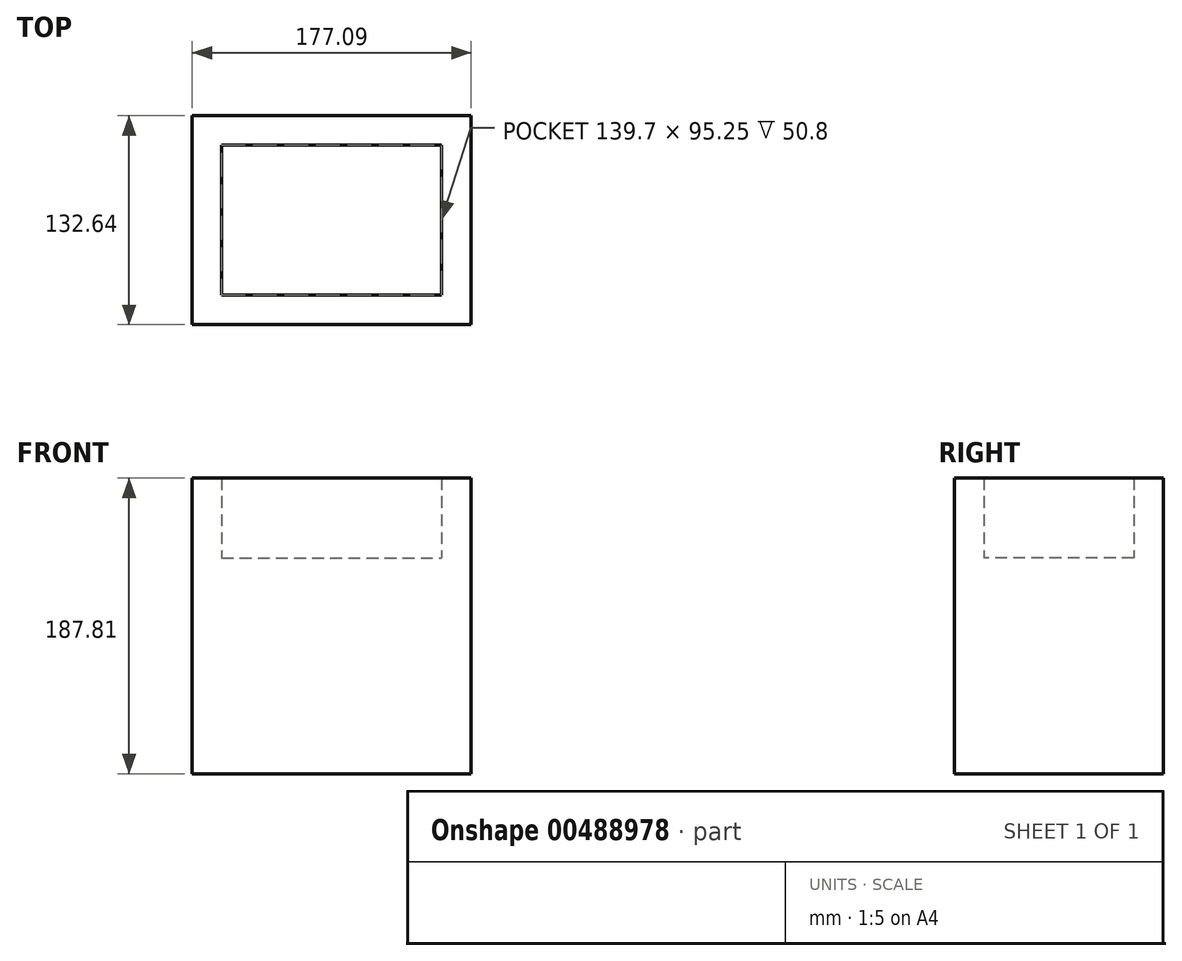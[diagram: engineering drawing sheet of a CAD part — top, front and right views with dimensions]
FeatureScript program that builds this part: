
annotation { "Feature Type Name" : "Feature", "Feature Type Description" : "" }
export const myFeature = defineFeature(function(context is Context, id is Id, definition is map)
    precondition{}
    {
        {
            var Q0;
            Q0=qCreatedBy(makeId("Top.planeOp"),FACE);
            var sketch = newSketch(context, id + "F0", { "sketchPlane" : qUnion([Q0])});
            skLineSegment(sketch, "E0", {"start": v(0, 0) * mm, "end": v(177.09, 0) * mm});
            skLineSegment(sketch, "E1", {"start": v(177.09, 0) * mm, "end": v(177.09, -132.64) * mm});
            skLineSegment(sketch, "E2", {"start": v(177.09, -132.64) * mm, "end": v(0, -132.64) * mm});
            skLineSegment(sketch, "E3", {"start": v(0, 0) * mm, "end": v(0, -132.64) * mm});
            skLineSegment(sketch, "E4", {"start": v(0, -113.94) * mm, "end": v(177.09, -113.94) * mm});
            skLineSegment(sketch, "E5", {"start": v(0, -18.7) * mm, "end": v(177.09, -18.7) * mm});
            skLineSegment(sketch, "E6", {"start": v(18.7, -18.7) * mm, "end": v(18.7, -113.94) * mm});
            skLineSegment(sketch, "E7", {"start": v(158.4, -18.7) * mm, "end": v(158.4, -113.94) * mm});
            skSolve(sketch);
        }
        {
            var Q0;
            {var subQ0=sQuery(id+"F0.wireOp",EDGE,"E6");Q0=makeQuery(id+"F0.imprint","IMPRINT",FACE,{"disambiguationData":[TD([[makeQuery(id+"F0.imprint","IMPRINT",EDGE,{"derivedFrom":subQ0}),1.0]])]});}
            extrude(context, id + "F1", {"entities" : qUnion([Q0]), "depth" : 137 * mm, "offsetDistance" : 25.4 * mm});
        }
        {
            var Q0;
            {var subQ4=sQuery(id+"F0.wireOp",EDGE,"E0");Q0=makeQuery(id+"F0.imprint","IMPRINT",FACE,{"disambiguationData":[TD([[makeQuery(id+"F0.imprint","IMPRINT",EDGE,{"derivedFrom":subQ4}),-1.0]])]});}
            var Q1;
            {var subQ5=sQuery(id+"F0.wireOp",EDGE,"E7");Q1=makeQuery(id+"F0.imprint","IMPRINT",FACE,{"disambiguationData":[TD([[makeQuery(id+"F0.imprint","IMPRINT",EDGE,{"derivedFrom":subQ5}),1.0]])]});}
            var Q2;
            {var subQ1=sQuery(id+"F0.wireOp",EDGE,"E2");Q2=makeQuery(id+"F0.imprint","IMPRINT",FACE,{"disambiguationData":[TD([[makeQuery(id+"F0.imprint","IMPRINT",EDGE,{"derivedFrom":subQ1}),-1.0]])]});}
            var Q3;
            {var subQ5=sQuery(id+"F0.wireOp",EDGE,"E6");Q3=makeQuery(id+"F0.imprint","IMPRINT",FACE,{"disambiguationData":[TD([[makeQuery(id+"F0.imprint","IMPRINT",EDGE,{"derivedFrom":subQ5}),-1.0]])]});}
            extrude(context, id + "F2", {"entities" : qUnion([Q0, Q1, Q2, Q3]), "operationType" : NewBodyOperationType.ADD, "depth" : 187.8 * mm, "offsetDistance" : 25.4 * mm});
        }
    });
